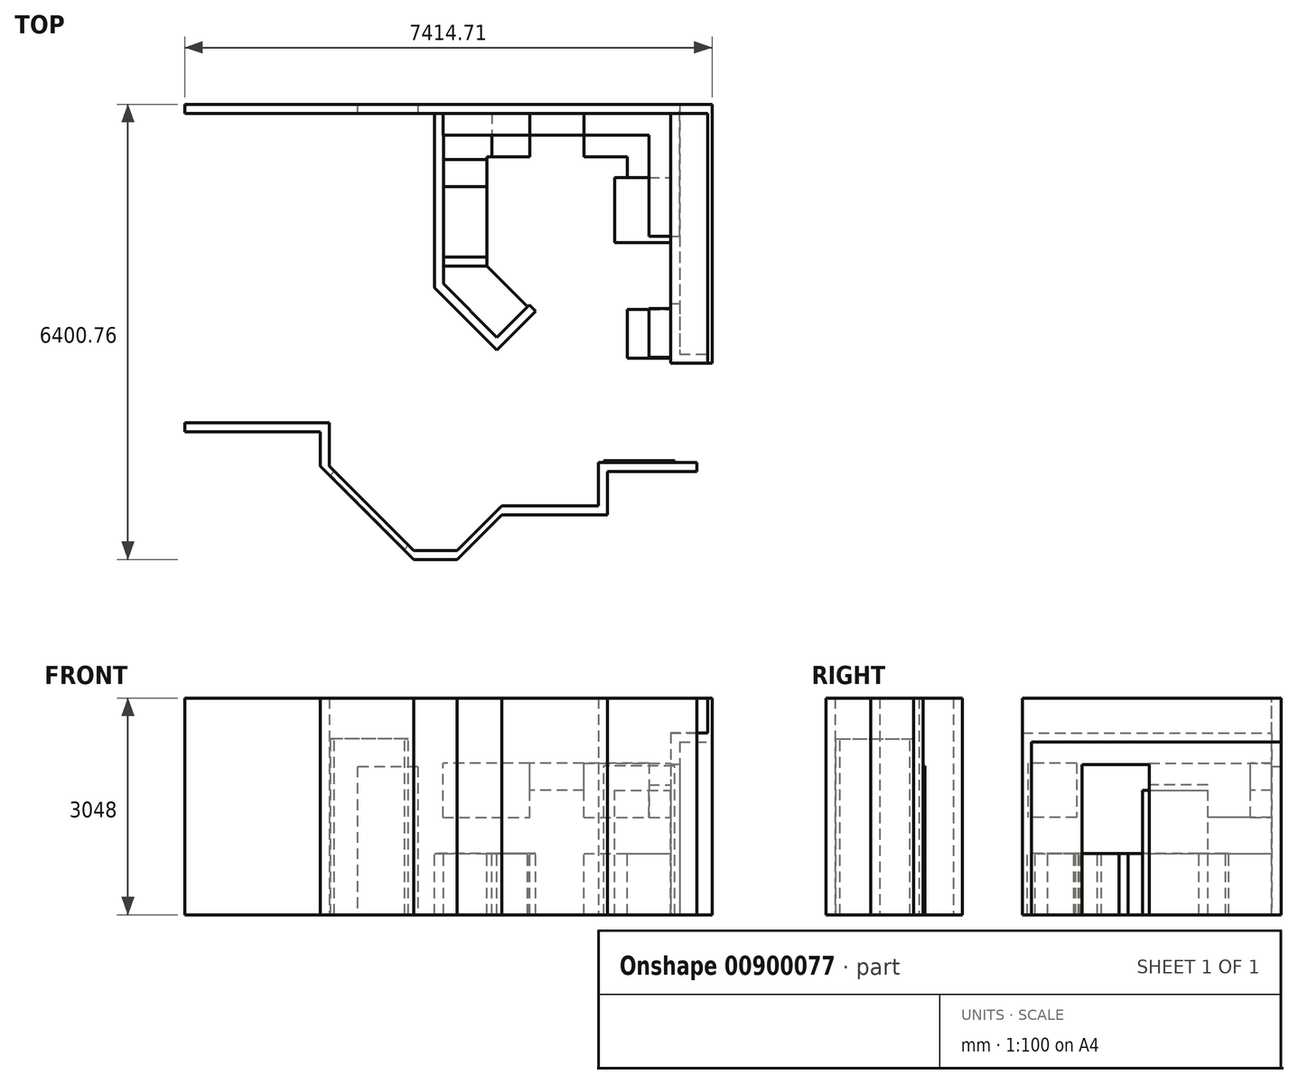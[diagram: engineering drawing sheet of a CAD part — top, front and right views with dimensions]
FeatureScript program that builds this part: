
annotation { "Feature Type Name" : "Feature", "Feature Type Description" : "" }
export const myFeature = defineFeature(function(context is Context, id is Id, definition is map)
    precondition{}
    {
        {
            var Q0;
            Q0=qCreatedBy(makeId("Top.planeOp"),FACE);
            var sketch = newSketch(context, id + "F0", { "sketchPlane" : qUnion([Q0])});
            skLineSegment(sketch, "E0.bottom", {"start": v(1769.95, -316.58) * mm, "end": v(-1786.05, -316.58) * mm});
            skLineSegment(sketch, "E0.top", {"start": v(1769.95, -189.58) * mm, "end": v(-1786.05, -189.58) * mm});
            skLineSegment(sketch, "E0.left", {"start": v(1769.95, -316.58) * mm, "end": v(1769.95, -189.58) * mm});
            skLineSegment(sketch, "E0.right", {"start": v(-1786.05, -316.58) * mm, "end": v(-1786.05, -189.58) * mm});
            skSolve(sketch);
        }
        {
            var Q0;
            Q0 = qSketchRegion(id + "F0", true);
            extrude(context, id + "F1", {"entities" : qUnion([Q0]), "depth" : 3048 * mm, "offsetDistance" : 25.4 * mm});
        }
        {
            var Q0;
            Q0=makeQuery(id+"F1.opExtrude","CAP_FACE",FACE,{"disambiguationData":[OSD([sQuery(id+"F0.wireOp",EDGE,"E0.bottom"),sQuery(id+"F0.wireOp",EDGE,"E0.top"),sQuery(id+"F0.wireOp",EDGE,"E0.left"),sQuery(id+"F0.wireOp",EDGE,"E0.right")])],"isStart":true});
            var sketch = newSketch(context, id + "F2", { "sketchPlane" : qUnion([Q0])});
            skLineSegment(sketch, "E1", {"start": v(1769.95, 316.58) * mm, "end": v(1769.95, 2043.78) * mm});
            skLineSegment(sketch, "E2", {"start": v(1769.95, 2043.78) * mm, "end": v(1896.95, 2043.78) * mm});
            skLineSegment(sketch, "E3", {"start": v(1896.95, 2043.78) * mm, "end": v(1896.95, 189.58) * mm});
            skLineSegment(sketch, "E4", {"start": v(1896.95, 189.58) * mm, "end": v(1769.95, 189.58) * mm});
            skLineSegment(sketch, "E5", {"start": v(1769.95, 189.58) * mm, "end": v(1769.95, 316.58) * mm});
            skSolve(sketch);
        }
        {
            var Q0;
            Q0=makeQuery(id+"F2.imprint","IMPRINT",FACE,{"disambiguationData":[TD([[makeQuery(id+"F2.imprint","IMPRINT",EDGE,{"derivedFrom":sQuery(id+"F2.wireOp",EDGE,"E1")}),-1.0]])]});
            var Q1;
            Q1=makeQuery(id+"F1.opExtrude","CAP_FACE",FACE,{"disambiguationData":[OSD([sQuery(id+"F0.wireOp",EDGE,"E0.bottom"),sQuery(id+"F0.wireOp",EDGE,"E0.top"),sQuery(id+"F0.wireOp",EDGE,"E0.left"),sQuery(id+"F0.wireOp",EDGE,"E0.right")])],"isStart":false});
            extrude(context, id + "F3", {"entities" : qUnion([Q0]), "operationType" : NewBodyOperationType.ADD, "endBound" : BoundingType.UP_TO_SURFACE, "oppositeDirection" : true, "depth" : 25.4 * mm, "endBoundEntityFace" : qUnion([Q1]), "offsetDistance" : 25.4 * mm});
        }
        {
            var Q0;
            Q0=makeQuery(id+"F3.boolean.opBoolean","MERGE",FACE,{"derivedFrom":[makeQuery(id+"F1.opExtrude","CAP_FACE",FACE,{"disambiguationData":[OSD([sQuery(id+"F0.wireOp",EDGE,"E0.bottom"),sQuery(id+"F0.wireOp",EDGE,"E0.top"),sQuery(id+"F0.wireOp",EDGE,"E0.left"),sQuery(id+"F0.wireOp",EDGE,"E0.right")])],"isStart":true}),makeQuery(id+"F3.opExtrude","CAP_FACE",FACE,{"disambiguationData":[OSD([sQuery(id+"F2.wireOp",EDGE,"E1"),sQuery(id+"F2.wireOp",EDGE,"E2"),sQuery(id+"F2.wireOp",EDGE,"E3"),sQuery(id+"F2.wireOp",EDGE,"E4"),sQuery(id+"F2.wireOp",EDGE,"E5")])],"isStart":true})]});
            var sketch = newSketch(context, id + "F4", { "sketchPlane" : qUnion([Q0])});
            skLineSegment(sketch, "E6", {"start": v(1769.95, 2043.78) * mm, "end": v(1769.95, 3936.08) * mm, "construction": true});
            skLineSegment(sketch, "E7", {"start": v(1896.95, 2043.78) * mm, "end": v(1896.95, 4648.91) * mm, "construction": true});
            skLineSegment(sketch, "E8.bottom", {"start": v(1769.95, 2989.93) * mm, "end": v(1896.95, 2989.93) * mm});
            skLineSegment(sketch, "E8.top", {"start": v(1769.95, 3828.13) * mm, "end": v(1896.95, 3828.13) * mm});
            skLineSegment(sketch, "E8.left", {"start": v(1769.95, 2989.93) * mm, "end": v(1769.95, 3828.13) * mm});
            skLineSegment(sketch, "E8.right", {"start": v(1896.95, 2989.93) * mm, "end": v(1896.95, 3828.13) * mm});
            skSolve(sketch);
        }
        {
            var Q0;
            Q0 = qSketchRegion(id + "F4", true);
            var Q1;
            Q1=makeQuery(id+"F3.boolean.opBoolean","MERGE",FACE,{"derivedFrom":[makeQuery(id+"F1.opExtrude","CAP_FACE",FACE,{"disambiguationData":[OSD([sQuery(id+"F0.wireOp",EDGE,"E0.bottom"),sQuery(id+"F0.wireOp",EDGE,"E0.top"),sQuery(id+"F0.wireOp",EDGE,"E0.left"),sQuery(id+"F0.wireOp",EDGE,"E0.right")])],"isStart":false}),makeQuery(id+"F3.opExtrude","CAP_FACE",FACE,{"disambiguationData":[OSD([sQuery(id+"F2.wireOp",EDGE,"E1"),sQuery(id+"F2.wireOp",EDGE,"E2"),sQuery(id+"F2.wireOp",EDGE,"E3"),sQuery(id+"F2.wireOp",EDGE,"E4"),sQuery(id+"F2.wireOp",EDGE,"E5")])],"isStart":false})]});
            extrude(context, id + "F5", {"entities" : qUnion([Q0]), "endBound" : BoundingType.UP_TO_SURFACE, "oppositeDirection" : true, "depth" : 25.4 * mm, "endBoundEntityFace" : qUnion([Q1]), "offsetDistance" : 25.4 * mm});
        }
        {
            var Q0;
            Q0=makeQuery(id+"F3.boolean.opBoolean","MERGE",FACE,{"derivedFrom":[makeQuery(id+"F1.opExtrude","CAP_FACE",FACE,{"disambiguationData":[OSD([sQuery(id+"F0.wireOp",EDGE,"E0.bottom"),sQuery(id+"F0.wireOp",EDGE,"E0.top"),sQuery(id+"F0.wireOp",EDGE,"E0.left"),sQuery(id+"F0.wireOp",EDGE,"E0.right")])],"isStart":true}),makeQuery(id+"F3.opExtrude","CAP_FACE",FACE,{"disambiguationData":[OSD([sQuery(id+"F2.wireOp",EDGE,"E1"),sQuery(id+"F2.wireOp",EDGE,"E2"),sQuery(id+"F2.wireOp",EDGE,"E3"),sQuery(id+"F2.wireOp",EDGE,"E4"),sQuery(id+"F2.wireOp",EDGE,"E5")])],"isStart":true})]});
            var sketch = newSketch(context, id + "F6", { "sketchPlane" : qUnion([Q0])});
            skLineSegment(sketch, "E9", {"start": v(1769.95, 2043.78) * mm, "end": v(1769.95, 3749.14) * mm, "construction": true});
            skLineSegment(sketch, "E10.bottom", {"start": v(1769.95, 5352.13) * mm, "end": v(753.95, 5352.13) * mm});
            skLineSegment(sketch, "E10.top", {"start": v(1769.95, 5225.13) * mm, "end": v(753.95, 5225.13) * mm});
            skLineSegment(sketch, "E10.left", {"start": v(1769.95, 5225.13) * mm, "end": v(1769.95, 5352.13) * mm});
            skLineSegment(sketch, "E10.right", {"start": v(753.95, 5225.13) * mm, "end": v(753.95, 5352.13) * mm});
            skSolve(sketch);
        }
        {
            var Q0;
            Q0=makeQuery(id+"F6.imprint","IMPRINT",FACE,{"disambiguationData":[TD([[makeQuery(id+"F6.imprint","IMPRINT",EDGE,{"derivedFrom":sQuery(id+"F6.wireOp",EDGE,"E10.bottom")}),1.0]])]});
            var Q1;
            Q1=makeQuery(id+"F3.boolean.opBoolean","MERGE",FACE,{"derivedFrom":[makeQuery(id+"F1.opExtrude","CAP_FACE",FACE,{"disambiguationData":[OSD([sQuery(id+"F0.wireOp",EDGE,"E0.bottom"),sQuery(id+"F0.wireOp",EDGE,"E0.top"),sQuery(id+"F0.wireOp",EDGE,"E0.left"),sQuery(id+"F0.wireOp",EDGE,"E0.right")])],"isStart":false}),makeQuery(id+"F3.opExtrude","CAP_FACE",FACE,{"disambiguationData":[OSD([sQuery(id+"F2.wireOp",EDGE,"E1"),sQuery(id+"F2.wireOp",EDGE,"E2"),sQuery(id+"F2.wireOp",EDGE,"E3"),sQuery(id+"F2.wireOp",EDGE,"E4"),sQuery(id+"F2.wireOp",EDGE,"E5")])],"isStart":false})]});
            extrude(context, id + "F7", {"entities" : qUnion([Q0]), "endBound" : BoundingType.UP_TO_SURFACE, "oppositeDirection" : true, "depth" : 25.4 * mm, "endBoundEntityFace" : qUnion([Q1]), "offsetDistance" : 25.4 * mm});
        }
        {
            var Q0;
            Q0=makeQuery(id+"F7.opExtrude","CAP_FACE",FACE,{"disambiguationData":[OSD([sQuery(id+"F6.wireOp",EDGE,"E10.bottom"),sQuery(id+"F6.wireOp",EDGE,"E10.top"),sQuery(id+"F6.wireOp",EDGE,"E10.left"),sQuery(id+"F6.wireOp",EDGE,"E10.right")])],"isStart":true});
            var sketch = newSketch(context, id + "F8", { "sketchPlane" : qUnion([Q0])});
            skLineSegment(sketch, "E11.bottom", {"start": v(753.95, 5225.13) * mm, "end": v(880.95, 5225.13) * mm});
            skLineSegment(sketch, "E11.top", {"start": v(753.95, 5834.73) * mm, "end": v(880.95, 5834.73) * mm});
            skLineSegment(sketch, "E11.left", {"start": v(753.95, 5225.13) * mm, "end": v(753.95, 5834.73) * mm});
            skLineSegment(sketch, "E11.right", {"start": v(880.95, 5225.13) * mm, "end": v(880.95, 5834.73) * mm});
            skLineSegment(sketch, "E12.bottom", {"start": v(880.95, 5834.73) * mm, "end": v(-604.95, 5834.73) * mm});
            skLineSegment(sketch, "E12.top", {"start": v(880.95, 5961.73) * mm, "end": v(-604.95, 5961.73) * mm});
            skLineSegment(sketch, "E12.left", {"start": v(880.95, 5834.73) * mm, "end": v(880.95, 5961.73) * mm});
            skLineSegment(sketch, "E12.right", {"start": v(-604.95, 5834.73) * mm, "end": v(-604.95, 5961.73) * mm});
            skLineSegment(sketch, "E13", {"start": v(-604.95, 5834.73) * mm, "end": v(-1233.57, 6463.34) * mm});
            skLineSegment(sketch, "E14", {"start": v(-1233.57, 6463.34) * mm, "end": v(-1843.17, 6463.34) * mm});
            skLineSegment(sketch, "E15", {"start": v(-1843.17, 6463.34) * mm, "end": v(-1843.17, 6590.34) * mm});
            skLineSegment(sketch, "E16", {"start": v(-1843.17, 6590.34) * mm, "end": v(-1233.57, 6590.34) * mm});
            skLineSegment(sketch, "E17", {"start": v(-1233.57, 6590.34) * mm, "end": v(-604.95, 5961.73) * mm});
            skLineSegment(sketch, "E18", {"start": v(-1843.17, 6463.34) * mm, "end": v(-3028.56, 5277.95) * mm});
            skLineSegment(sketch, "E19", {"start": v(-3028.56, 5277.95) * mm, "end": v(-3028.56, 4668.35) * mm});
            skLineSegment(sketch, "E20", {"start": v(-3028.56, 4668.35) * mm, "end": v(-5060.56, 4668.35) * mm});
            skLineSegment(sketch, "E21", {"start": v(-5060.56, 4668.35) * mm, "end": v(-5060.56, 4795.35) * mm});
            skLineSegment(sketch, "E22", {"start": v(-5060.56, 4795.35) * mm, "end": v(-3155.56, 4795.35) * mm});
            skLineSegment(sketch, "E23", {"start": v(-3155.56, 4795.35) * mm, "end": v(-3155.56, 5277.95) * mm});
            skLineSegment(sketch, "E24", {"start": v(-3155.56, 5277.95) * mm, "end": v(-1843.17, 6590.34) * mm});
            skSolve(sketch);
        }
        {
            var Q0;
            Q0=makeQuery(id+"F8.imprint","IMPRINT",FACE,{"disambiguationData":[TD([[makeQuery(id+"F8.imprint","IMPRINT",EDGE,{"derivedFrom":sQuery(id+"F8.wireOp",EDGE,"E15")}),1.0]])]});
            var Q1;
            Q1=makeQuery(id+"F8.imprint","IMPRINT",FACE,{"disambiguationData":[TD([[makeQuery(id+"F8.imprint","IMPRINT",EDGE,{"derivedFrom":sQuery(id+"F8.wireOp",EDGE,"E12.right")}),1.0]])]});
            var Q2;
            Q2=makeQuery(id+"F8.imprint","IMPRINT",FACE,{"disambiguationData":[TD([[makeQuery(id+"F8.imprint","IMPRINT",EDGE,{"derivedFrom":sQuery(id+"F8.wireOp",EDGE,"E12.top")}),1.0]])]});
            var Q3;
            {var subQ0=sQuery(id+"F8.wireOp",EDGE,"E11.left");var subQ1=makeQuery(id+"F7.opExtrude","CAP_EDGE",EDGE,{"disambiguationData":[OSD([sQuery(id+"F6.wireOp",EDGE,"E10.bottom")])],"isStart":true});var subQ2=makeQuery(id+"F8.imprint","INTERSECT",VERTEX,{"derivedFrom":[subQ1,subQ0]});Q3=makeQuery(id+"F8.imprint","IMPRINT",FACE,{"disambiguationData":[TD([[makeQuery(id+"F8.imprint","IMPRINT",EDGE,{"disambiguationData":[TD([[subQ2,-1.0]])],"derivedFrom":subQ0}),-1.0]])]});}
            var Q4;
            Q4=makeQuery(id+"F5.opExtrude","CAP_FACE",FACE,{"disambiguationData":[OSD([sQuery(id+"F4.wireOp",EDGE,"E8.bottom"),sQuery(id+"F4.wireOp",EDGE,"E8.top"),sQuery(id+"F4.wireOp",EDGE,"E8.left"),sQuery(id+"F4.wireOp",EDGE,"E8.right")])],"isStart":false});
            extrude(context, id + "F9", {"entities" : qUnion([Q0, Q1, Q2, Q3]), "operationType" : NewBodyOperationType.ADD, "endBound" : BoundingType.UP_TO_SURFACE, "oppositeDirection" : true, "depth" : 25.4 * mm, "endBoundEntityFace" : qUnion([Q4]), "offsetDistance" : 25.4 * mm});
        }
        {
            var Q0;
            {var subQ0=sQuery(id+"F6.wireOp",EDGE,"E10.bottom");Q0=makeQuery(id+"F9.boolean.opBoolean","MERGE",FACE,{"derivedFrom":[makeQuery(id+"F7.opExtrude","CAP_FACE",FACE,{"disambiguationData":[OSD([subQ0,sQuery(id+"F6.wireOp",EDGE,"E10.top"),sQuery(id+"F6.wireOp",EDGE,"E10.left"),sQuery(id+"F6.wireOp",EDGE,"E10.right")])],"isStart":true}),makeQuery(id+"F9.opExtrude","CAP_FACE",FACE,{"disambiguationData":[OSD([subQ0,sQuery(id+"F8.wireOp",EDGE,"E11.left"),sQuery(id+"F8.wireOp",EDGE,"E11.right"),sQuery(id+"F8.wireOp",EDGE,"E12.bottom"),sQuery(id+"F8.wireOp",EDGE,"E12.top"),sQuery(id+"F8.wireOp",EDGE,"E12.left"),sQuery(id+"F8.wireOp",EDGE,"E13"),sQuery(id+"F8.wireOp",EDGE,"E14"),sQuery(id+"F8.wireOp",EDGE,"E16"),sQuery(id+"F8.wireOp",EDGE,"E17"),sQuery(id+"F8.wireOp",EDGE,"E18"),sQuery(id+"F8.wireOp",EDGE,"E19"),sQuery(id+"F8.wireOp",EDGE,"E20"),sQuery(id+"F8.wireOp",EDGE,"E21"),sQuery(id+"F8.wireOp",EDGE,"E22"),sQuery(id+"F8.wireOp",EDGE,"E23"),sQuery(id+"F8.wireOp",EDGE,"E24")])],"isStart":true})]});}
            var sketch = newSketch(context, id + "F10", { "sketchPlane" : qUnion([Q0])});
            skLineSegment(sketch, "E25.bottom", {"start": v(1769.95, 5225.13) * mm, "end": v(2138.25, 5225.13) * mm});
            skLineSegment(sketch, "E25.top", {"start": v(1769.95, 5352.13) * mm, "end": v(2138.25, 5352.13) * mm});
            skLineSegment(sketch, "E25.left", {"start": v(1769.95, 5225.13) * mm, "end": v(1769.95, 5352.13) * mm});
            skLineSegment(sketch, "E25.right", {"start": v(2138.25, 5225.13) * mm, "end": v(2138.25, 5352.13) * mm});
            skSolve(sketch);
        }
        {
            var Q0;
            Q0=makeQuery(id+"F10.imprint","IMPRINT",FACE,{"disambiguationData":[TD([[makeQuery(id+"F10.imprint","IMPRINT",EDGE,{"derivedFrom":sQuery(id+"F10.wireOp",EDGE,"E25.bottom")}),1.0]])]});
            var Q1;
            {var subQ0=sQuery(id+"F6.wireOp",EDGE,"E10.bottom");Q1=makeQuery(id+"F9.boolean.opBoolean","MERGE",FACE,{"derivedFrom":[makeQuery(id+"F7.opExtrude","CAP_FACE",FACE,{"disambiguationData":[OSD([subQ0,sQuery(id+"F6.wireOp",EDGE,"E10.top"),sQuery(id+"F6.wireOp",EDGE,"E10.left"),sQuery(id+"F6.wireOp",EDGE,"E10.right")])],"isStart":false}),makeQuery(id+"F9.opExtrude","CAP_FACE",FACE,{"disambiguationData":[OSD([subQ0,sQuery(id+"F8.wireOp",EDGE,"E11.left"),sQuery(id+"F8.wireOp",EDGE,"E11.right"),sQuery(id+"F8.wireOp",EDGE,"E12.bottom"),sQuery(id+"F8.wireOp",EDGE,"E12.top"),sQuery(id+"F8.wireOp",EDGE,"E12.left"),sQuery(id+"F8.wireOp",EDGE,"E13"),sQuery(id+"F8.wireOp",EDGE,"E14"),sQuery(id+"F8.wireOp",EDGE,"E16"),sQuery(id+"F8.wireOp",EDGE,"E17"),sQuery(id+"F8.wireOp",EDGE,"E18"),sQuery(id+"F8.wireOp",EDGE,"E19"),sQuery(id+"F8.wireOp",EDGE,"E20"),sQuery(id+"F8.wireOp",EDGE,"E21"),sQuery(id+"F8.wireOp",EDGE,"E22"),sQuery(id+"F8.wireOp",EDGE,"E23"),sQuery(id+"F8.wireOp",EDGE,"E24")])],"isStart":false})]});}
            extrude(context, id + "F11", {"entities" : qUnion([Q0]), "operationType" : NewBodyOperationType.ADD, "endBound" : BoundingType.UP_TO_SURFACE, "oppositeDirection" : true, "depth" : 25.4 * mm, "endBoundEntityFace" : qUnion([Q1]), "offsetDistance" : 25.4 * mm});
        }
        {
            var Q0;
            Q0=makeQuery(id+"F11.boolean.opBoolean","MERGE",FACE,{"derivedFrom":[makeQuery(id+"F7.opExtrude","SWEPT_FACE",FACE,{"disambiguationData":[OSD([sQuery(id+"F6.wireOp",EDGE,"E10.top")])]}),makeQuery(id+"F11.opExtrude","SWEPT_FACE",FACE,{"disambiguationData":[OSD([sQuery(id+"F10.wireOp",EDGE,"E25.bottom")])]})]});
            var sketch = newSketch(context, id + "F12", { "sketchPlane" : qUnion([Q0])});
            skLineSegment(sketch, "E26.bottom", {"start": v(-1827.1, 0) * mm, "end": v(-830.15, 0) * mm});
            skLineSegment(sketch, "E26.top", {"start": v(-1827.1, 2095.5) * mm, "end": v(-830.15, 2095.5) * mm});
            skLineSegment(sketch, "E26.left", {"start": v(-1827.1, 0) * mm, "end": v(-1827.1, 2095.5) * mm});
            skLineSegment(sketch, "E26.right", {"start": v(-830.15, 0) * mm, "end": v(-830.15, 2095.5) * mm});
            skSolve(sketch);
        }
        {
            var Q0;
            Q0 = qSketchRegion(id + "F12", true);
            extrude(context, id + "F13", {"entities" : qUnion([Q0]), "operationType" : NewBodyOperationType.ADD, "depth" : 25.4 * mm, "offsetDistance" : 25.4 * mm});
        }
        {
            var Q0;
            Q0=makeQuery(id+"F1.opExtrude","SWEPT_FACE",FACE,{"disambiguationData":[OSD([sQuery(id+"F0.wireOp",EDGE,"E0.bottom")])]});
            var sketch = newSketch(context, id + "F14", { "sketchPlane" : qUnion([Q0])});
            skLineSegment(sketch, "E27.bottom", {"start": v(-1786.05, 3048) * mm, "end": v(-2636.95, 3048) * mm});
            skLineSegment(sketch, "E27.top", {"start": v(-1786.05, 2082.8) * mm, "end": v(-2636.95, 2082.8) * mm});
            skLineSegment(sketch, "E27.left", {"start": v(-1786.05, 3048) * mm, "end": v(-1786.05, 2082.8) * mm});
            skLineSegment(sketch, "E27.right", {"start": v(-2636.95, 3048) * mm, "end": v(-2636.95, 2082.8) * mm});
            skSolve(sketch);
        }
        {
            var Q0;
            Q0=makeQuery(id+"F14.imprint","IMPRINT",FACE,{"disambiguationData":[TD([[makeQuery(id+"F14.imprint","IMPRINT",EDGE,{"derivedFrom":sQuery(id+"F14.wireOp",EDGE,"E27.bottom")}),1.0]])]});
            var Q1;
            Q1=makeQuery(id+"F3.boolean.opBoolean","MERGE",FACE,{"derivedFrom":[makeQuery(id+"F1.opExtrude","SWEPT_FACE",FACE,{"disambiguationData":[OSD([sQuery(id+"F0.wireOp",EDGE,"E0.top")])]}),makeQuery(id+"F3.opExtrude","SWEPT_FACE",FACE,{"disambiguationData":[OSD([sQuery(id+"F2.wireOp",EDGE,"E4")])]})]});
            extrude(context, id + "F15", {"entities" : qUnion([Q0]), "operationType" : NewBodyOperationType.ADD, "endBound" : BoundingType.UP_TO_SURFACE, "oppositeDirection" : true, "depth" : 25.4 * mm, "endBoundEntityFace" : qUnion([Q1]), "offsetDistance" : 25.4 * mm});
        }
        {
            var Q0;
            Q0=makeQuery(id+"F15.opExtrude","SWEPT_FACE",FACE,{"disambiguationData":[OSD([sQuery(id+"F14.wireOp",EDGE,"E27.right")])]});
            var sketch = newSketch(context, id + "F16", { "sketchPlane" : qUnion([Q0])});
            skLineSegment(sketch, "E28.bottom", {"start": v(189.58, 3048) * mm, "end": v(316.58, 3048) * mm});
            skLineSegment(sketch, "E28.top", {"start": v(189.58, 0) * mm, "end": v(316.58, 0) * mm});
            skLineSegment(sketch, "E28.left", {"start": v(189.58, 3048) * mm, "end": v(189.58, 0) * mm});
            skLineSegment(sketch, "E28.right", {"start": v(316.58, 3048) * mm, "end": v(316.58, 0) * mm});
            skSolve(sketch);
        }
        {
            var Q0;
            {var subQ0=sQuery(id+"F16.wireOp",EDGE,"E28.bottom");Q0=makeQuery(id+"F16.imprint","IMPRINT",FACE,{"disambiguationData":[TD([[makeQuery(id+"F16.imprint","IMPRINT",EDGE,{"derivedFrom":subQ0}),-1.0]])]});}
            var Q1;
            {var subQ0=sQuery(id+"F16.wireOp",EDGE,"E28.top");Q1=makeQuery(id+"F16.imprint","IMPRINT",FACE,{"disambiguationData":[TD([[makeQuery(id+"F16.imprint","IMPRINT",EDGE,{"derivedFrom":subQ0}),1.0]])]});}
            var Q2;
            Q2=makeQuery(id+"F9.opExtrude","SWEPT_FACE",FACE,{"disambiguationData":[OSD([sQuery(id+"F8.wireOp",EDGE,"E21")])]});
            extrude(context, id + "F17", {"entities" : qUnion([Q0, Q1]), "operationType" : NewBodyOperationType.ADD, "endBound" : BoundingType.UP_TO_SURFACE, "depth" : 25.4 * mm, "endBoundEntityFace" : qUnion([Q2]), "offsetDistance" : 25.4 * mm});
        }
        {
            var Q0;
            Q0=makeQuery(id+"F3.opExtrude","SWEPT_FACE",FACE,{"disambiguationData":[OSD([sQuery(id+"F2.wireOp",EDGE,"E1"),sQuery(id+"F2.wireOp",EDGE,"E5")])]});
            var sketch = newSketch(context, id + "F18", { "sketchPlane" : qUnion([Q0])});
            skLineSegment(sketch, "E29.bottom", {"start": v(2043.78, 3048) * mm, "end": v(3103.37, 3048) * mm});
            skLineSegment(sketch, "E29.top", {"start": v(2043.78, 2114.55) * mm, "end": v(3103.37, 2114.55) * mm});
            skLineSegment(sketch, "E29.left", {"start": v(2043.78, 3048) * mm, "end": v(2043.78, 2114.55) * mm});
            skLineSegment(sketch, "E29.right", {"start": v(3103.37, 3048) * mm, "end": v(3103.37, 2114.55) * mm});
            skSolve(sketch);
        }
        {
            var Q0;
            Q0=makeQuery(id+"F18.imprint","IMPRINT",FACE,{"disambiguationData":[TD([[makeQuery(id+"F18.imprint","IMPRINT",EDGE,{"derivedFrom":sQuery(id+"F18.wireOp",EDGE,"E29.bottom")}),-1.0]])]});
            var Q1;
            Q1=makeQuery(id+"F5.opExtrude","SWEPT_FACE",FACE,{"disambiguationData":[OSD([sQuery(id+"F4.wireOp",EDGE,"E8.right")])]});
            extrude(context, id + "F19", {"entities" : qUnion([Q0]), "endBound" : BoundingType.UP_TO_SURFACE, "oppositeDirection" : true, "depth" : 25.4 * mm, "endBoundEntityFace" : qUnion([Q1]), "offsetDistance" : 25.4 * mm});
        }
        {
            var Q0;
            Q0=makeQuery(id+"F1.opExtrude","SWEPT_BODY",BODY,{"disambiguationData":[OSD([sQuery(id+"F0.wireOp",EDGE,"E0.bottom"),sQuery(id+"F0.wireOp",EDGE,"E0.top"),sQuery(id+"F0.wireOp",EDGE,"E0.left"),sQuery(id+"F0.wireOp",EDGE,"E0.right")])]});
            var Q1;
            Q1=makeQuery(id+"F19.opExtrude","SWEPT_BODY",BODY,{"disambiguationData":[OSD([sQuery(id+"F18.wireOp",EDGE,"E29.bottom"),sQuery(id+"F18.wireOp",EDGE,"E29.top"),sQuery(id+"F18.wireOp",EDGE,"E29.left"),sQuery(id+"F18.wireOp",EDGE,"E29.right")])]});
            var Q2;
            Q2=makeQuery(id+"F5.opExtrude","SWEPT_BODY",BODY,{"disambiguationData":[OSD([sQuery(id+"F4.wireOp",EDGE,"E8.bottom"),sQuery(id+"F4.wireOp",EDGE,"E8.top"),sQuery(id+"F4.wireOp",EDGE,"E8.left"),sQuery(id+"F4.wireOp",EDGE,"E8.right")])]});
            booleanBodies(context, id + "F20", {"operationType" : BooleanOperationType.UNION, "tools" : qUnion([Q0, Q1, Q2])});
        }
        {
            var Q0;
            Q0=makeQuery(id+"F20.opBoolean","MERGE",FACE,{"derivedFrom":[makeQuery(id+"F5.opExtrude","CAP_FACE",FACE,{"disambiguationData":[OSD([sQuery(id+"F4.wireOp",EDGE,"E8.bottom"),sQuery(id+"F4.wireOp",EDGE,"E8.top"),sQuery(id+"F4.wireOp",EDGE,"E8.left"),sQuery(id+"F4.wireOp",EDGE,"E8.right")])],"isStart":false}),makeQuery(id+"F17.boolean.opBoolean","MERGE",FACE,{"derivedFrom":[makeQuery(id+"F15.boolean.opBoolean","MERGE",FACE,{"derivedFrom":[makeQuery(id+"F3.boolean.opBoolean","MERGE",FACE,{"derivedFrom":[makeQuery(id+"F1.opExtrude","CAP_FACE",FACE,{"disambiguationData":[OSD([sQuery(id+"F0.wireOp",EDGE,"E0.bottom"),sQuery(id+"F0.wireOp",EDGE,"E0.top"),sQuery(id+"F0.wireOp",EDGE,"E0.left"),sQuery(id+"F0.wireOp",EDGE,"E0.right")])],"isStart":false}),makeQuery(id+"F3.opExtrude","CAP_FACE",FACE,{"disambiguationData":[OSD([sQuery(id+"F2.wireOp",EDGE,"E1"),sQuery(id+"F2.wireOp",EDGE,"E2"),sQuery(id+"F2.wireOp",EDGE,"E3"),sQuery(id+"F2.wireOp",EDGE,"E4"),sQuery(id+"F2.wireOp",EDGE,"E5")])],"isStart":false})]}),makeQuery(id+"F15.opExtrude","SWEPT_FACE",FACE,{"disambiguationData":[OSD([sQuery(id+"F14.wireOp",EDGE,"E27.bottom")])]})]}),makeQuery(id+"F17.opExtrude","SWEPT_FACE",FACE,{"disambiguationData":[OSD([sQuery(id+"F16.wireOp",EDGE,"E28.bottom")])]})]}),makeQuery(id+"F19.opExtrude","SWEPT_FACE",FACE,{"disambiguationData":[OSD([sQuery(id+"F18.wireOp",EDGE,"E29.bottom")])]})]});
            var sketch = newSketch(context, id + "F21", { "sketchPlane" : qUnion([Q0])});
            skLineSegment(sketch, "E30.bottom", {"start": v(1769.95, -3828.13) * mm, "end": v(2354.15, -3828.13) * mm});
            skLineSegment(sketch, "E30.top", {"start": v(1769.95, -3701.13) * mm, "end": v(2354.15, -3701.13) * mm});
            skLineSegment(sketch, "E30.left", {"start": v(1769.95, -3828.13) * mm, "end": v(1769.95, -3701.13) * mm});
            skLineSegment(sketch, "E30.right", {"start": v(2354.15, -3828.13) * mm, "end": v(2354.15, -3701.13) * mm});
            skSolve(sketch);
        }
        {
            var Q0;
            {var subQ3=sQuery(id+"F21.wireOp",EDGE,"E30.right");Q0=makeQuery(id+"F21.imprint","IMPRINT",FACE,{"disambiguationData":[TD([[makeQuery(id+"F21.imprint","IMPRINT",EDGE,{"derivedFrom":subQ3}),1.0]])]});}
            var Q1;
            Q1=makeQuery(id+"F5.opExtrude","CAP_FACE",FACE,{"disambiguationData":[OSD([sQuery(id+"F4.wireOp",EDGE,"E8.bottom"),sQuery(id+"F4.wireOp",EDGE,"E8.top"),sQuery(id+"F4.wireOp",EDGE,"E8.left"),sQuery(id+"F4.wireOp",EDGE,"E8.right")])],"isStart":true});
            extrude(context, id + "F22", {"entities" : qUnion([Q0]), "operationType" : NewBodyOperationType.ADD, "endBound" : BoundingType.UP_TO_SURFACE, "oppositeDirection" : true, "depth" : 25.4 * mm, "endBoundEntityFace" : qUnion([Q1]), "offsetDistance" : 25.4 * mm});
        }
        {
            var Q0;
            Q0=makeQuery(id+"F19.opExtrude","SWEPT_FACE",FACE,{"disambiguationData":[OSD([sQuery(id+"F18.wireOp",EDGE,"E29.top")])]});
            cPlane(context, id + "F23", {"entities" : qUnion([Q0]), "cplaneType" : CPlaneType.OFFSET, "offset" : 444.5 * mm, "oppositeDirection" : true, "width" : 152.4 * mm, "height" : 152.4 * mm});
        }
        {
            var Q0;
            Q0=qCreatedBy(id+"F23.planeOp",FACE);
            var sketch = newSketch(context, id + "F24", { "sketchPlane" : qUnion([Q0])});
            skLineSegment(sketch, "E31.bottom", {"start": v(1769.95, 3828.13) * mm, "end": v(2290.65, 3828.13) * mm});
            skLineSegment(sketch, "E31.top", {"start": v(1769.95, 189.58) * mm, "end": v(2290.65, 189.58) * mm});
            skLineSegment(sketch, "E31.left", {"start": v(1769.95, 3828.13) * mm, "end": v(1769.95, 189.58) * mm});
            skLineSegment(sketch, "E31.right", {"start": v(2290.65, 3828.13) * mm, "end": v(2290.65, 189.58) * mm});
            skSolve(sketch);
        }
        {
            var Q0;
            Q0=makeQuery(id+"F24.imprint","IMPRINT",FACE,{"disambiguationData":[TD([[makeQuery(id+"F24.imprint","IMPRINT",EDGE,{"derivedFrom":sQuery(id+"F24.wireOp",EDGE,"E31.bottom")}),-1.0]])]});
            extrude(context, id + "F25", {"entities" : qUnion([Q0]), "operationType" : NewBodyOperationType.ADD, "depth" : 127 * mm, "offsetDistance" : 25.4 * mm});
        }
        {
            var Q0;
            Q0=makeQuery(id+"F25.opExtrude","SWEPT_FACE",FACE,{"disambiguationData":[OSD([sQuery(id+"F24.wireOp",EDGE,"E31.right")])]});
            var sketch = newSketch(context, id + "F26", { "sketchPlane" : qUnion([Q0])});
            skLineSegment(sketch, "E32.bottom", {"start": v(-4015.8, 2559.05) * mm, "end": v(-316.58, 2559.05) * mm});
            skLineSegment(sketch, "E32.top", {"start": v(-4015.8, 4185.07) * mm, "end": v(-316.58, 4185.07) * mm});
            skLineSegment(sketch, "E32.left", {"start": v(-4015.8, 2559.05) * mm, "end": v(-4015.8, 4185.07) * mm});
            skLineSegment(sketch, "E32.right", {"start": v(-316.58, 2559.05) * mm, "end": v(-316.58, 4185.07) * mm});
            skSolve(sketch);
        }
        {
            var Q0;
            Q0 = qSketchRegion(id + "F26", true);
            extrude(context, id + "F27", {"entities" : qUnion([Q0]), "operationType" : NewBodyOperationType.REMOVE, "oppositeDirection" : true, "depth" : 1270 * mm, "offsetDistance" : 25.4 * mm});
        }
        {
            var Q0;
            Q0=makeQuery(id+"F25.boolean.opBoolean","MERGE",FACE,{"derivedFrom":[makeQuery(id+"F17.boolean.opBoolean","MERGE",FACE,{"derivedFrom":[makeQuery(id+"F15.boolean.opBoolean","MERGE",FACE,{"derivedFrom":[makeQuery(id+"F3.boolean.opBoolean","MERGE",FACE,{"derivedFrom":[makeQuery(id+"F1.opExtrude","SWEPT_FACE",FACE,{"disambiguationData":[OSD([sQuery(id+"F0.wireOp",EDGE,"E0.top")])]}),makeQuery(id+"F3.opExtrude","SWEPT_FACE",FACE,{"disambiguationData":[OSD([sQuery(id+"F2.wireOp",EDGE,"E4")])]})]}),makeQuery(id+"F15.opExtrude","CAP_FACE",FACE,{"disambiguationData":[OSD([sQuery(id+"F14.wireOp",EDGE,"E27.bottom"),sQuery(id+"F14.wireOp",EDGE,"E27.top"),sQuery(id+"F14.wireOp",EDGE,"E27.left"),sQuery(id+"F14.wireOp",EDGE,"E27.right")])],"isStart":false})]}),makeQuery(id+"F17.opExtrude","SWEPT_FACE",FACE,{"disambiguationData":[OSD([sQuery(id+"F16.wireOp",EDGE,"E28.left")])]})]}),makeQuery(id+"F25.opExtrude","SWEPT_FACE",FACE,{"disambiguationData":[OSD([sQuery(id+"F24.wireOp",EDGE,"E31.top")])]})]});
            var sketch = newSketch(context, id + "F28", { "sketchPlane" : qUnion([Q0])});
            skLineSegment(sketch, "E33.bottom", {"start": v(-1896.95, 3048) * mm, "end": v(-2354.15, 3048) * mm});
            skLineSegment(sketch, "E33.top", {"start": v(-1896.95, 2432.05) * mm, "end": v(-2354.15, 2432.05) * mm});
            skLineSegment(sketch, "E33.left", {"start": v(-1896.95, 3048) * mm, "end": v(-1896.95, 2432.05) * mm});
            skLineSegment(sketch, "E33.right", {"start": v(-2354.15, 3048) * mm, "end": v(-2354.15, 2432.05) * mm});
            skSolve(sketch);
        }
        {
            var Q0;
            {var subQ1=sQuery(id+"F28.wireOp",EDGE,"E33.bottom");Q0=makeQuery(id+"F28.imprint","IMPRINT",FACE,{"disambiguationData":[TD([[makeQuery(id+"F28.imprint","IMPRINT",EDGE,{"derivedFrom":subQ1}),1.0]])]});}
            var Q1;
            Q1=makeQuery(id+"F27.boolean.opBoolean","MERGE",FACE,{"derivedFrom":[makeQuery(id+"F17.boolean.opBoolean","MERGE",FACE,{"derivedFrom":[makeQuery(id+"F15.boolean.opBoolean","MERGE",FACE,{"derivedFrom":[makeQuery(id+"F1.opExtrude","SWEPT_FACE",FACE,{"disambiguationData":[OSD([sQuery(id+"F0.wireOp",EDGE,"E0.bottom")])]}),makeQuery(id+"F15.opExtrude","CAP_FACE",FACE,{"disambiguationData":[OSD([sQuery(id+"F14.wireOp",EDGE,"E27.bottom"),sQuery(id+"F14.wireOp",EDGE,"E27.top"),sQuery(id+"F14.wireOp",EDGE,"E27.left"),sQuery(id+"F14.wireOp",EDGE,"E27.right")])],"isStart":true})]}),makeQuery(id+"F17.opExtrude","SWEPT_FACE",FACE,{"disambiguationData":[OSD([sQuery(id+"F16.wireOp",EDGE,"E28.right")])]})]})],"fromTools":[makeQuery(id+"F27.opExtrude","SWEPT_FACE",FACE,{"disambiguationData":[OSD([sQuery(id+"F26.wireOp",EDGE,"E32.right")])]})]});
            extrude(context, id + "F29", {"entities" : qUnion([Q0]), "operationType" : NewBodyOperationType.ADD, "endBound" : BoundingType.UP_TO_SURFACE, "oppositeDirection" : true, "depth" : 25.4 * mm, "endBoundEntityFace" : qUnion([Q1]), "offsetDistance" : 25.4 * mm});
        }
        {
            var Q0;
            {var subQ0=sQuery(id+"F24.wireOp",EDGE,"E31.top");Q0=makeQuery(id+"F29.boolean.opBoolean","MERGE",FACE,{"derivedFrom":[makeQuery(id+"F25.boolean.opBoolean","MERGE",FACE,{"derivedFrom":[makeQuery(id+"F17.boolean.opBoolean","MERGE",FACE,{"derivedFrom":[makeQuery(id+"F15.boolean.opBoolean","MERGE",FACE,{"derivedFrom":[makeQuery(id+"F3.boolean.opBoolean","MERGE",FACE,{"derivedFrom":[makeQuery(id+"F1.opExtrude","SWEPT_FACE",FACE,{"disambiguationData":[OSD([sQuery(id+"F0.wireOp",EDGE,"E0.top")])]}),makeQuery(id+"F3.opExtrude","SWEPT_FACE",FACE,{"disambiguationData":[OSD([sQuery(id+"F2.wireOp",EDGE,"E4")])]})]}),makeQuery(id+"F15.opExtrude","CAP_FACE",FACE,{"disambiguationData":[OSD([sQuery(id+"F14.wireOp",EDGE,"E27.bottom"),sQuery(id+"F14.wireOp",EDGE,"E27.top"),sQuery(id+"F14.wireOp",EDGE,"E27.left"),sQuery(id+"F14.wireOp",EDGE,"E27.right")])],"isStart":false})]}),makeQuery(id+"F17.opExtrude","SWEPT_FACE",FACE,{"disambiguationData":[OSD([sQuery(id+"F16.wireOp",EDGE,"E28.left")])]})]}),makeQuery(id+"F25.opExtrude","SWEPT_FACE",FACE,{"disambiguationData":[OSD([subQ0])]})]}),makeQuery(id+"F29.opExtrude","CAP_FACE",FACE,{"disambiguationData":[OSD([subQ0,sQuery(id+"F24.wireOp",EDGE,"E31.right"),sQuery(id+"F28.wireOp",EDGE,"E33.bottom"),sQuery(id+"F28.wireOp",EDGE,"E33.top"),sQuery(id+"F28.wireOp",EDGE,"E33.left"),sQuery(id+"F28.wireOp",EDGE,"E33.right")])],"isStart":true})]});}
            var sketch = newSketch(context, id + "F30", { "sketchPlane" : qUnion([Q0])});
            skLineSegment(sketch, "E34.bottom", {"start": v(-2354.15, 3048) * mm, "end": v(-2290.65, 3048) * mm});
            skLineSegment(sketch, "E34.top", {"start": v(-2354.15, 2432.05) * mm, "end": v(-2290.65, 2432.05) * mm});
            skLineSegment(sketch, "E34.left", {"start": v(-2354.15, 3048) * mm, "end": v(-2354.15, 2432.05) * mm});
            skLineSegment(sketch, "E34.right", {"start": v(-2290.65, 3048) * mm, "end": v(-2290.65, 2432.05) * mm});
            skSolve(sketch);
        }
        {
            var Q0;
            Q0=makeQuery(id+"F30.imprint","IMPRINT",FACE,{"disambiguationData":[TD([[makeQuery(id+"F30.imprint","IMPRINT",EDGE,{"derivedFrom":sQuery(id+"F30.wireOp",EDGE,"E34.bottom")}),-1.0]])]});
            var Q1;
            Q1=makeQuery(id+"F22.opExtrude","SWEPT_FACE",FACE,{"disambiguationData":[OSD([sQuery(id+"F21.wireOp",EDGE,"E30.top")])]});
            extrude(context, id + "F31", {"entities" : qUnion([Q0]), "operationType" : NewBodyOperationType.ADD, "endBound" : BoundingType.UP_TO_SURFACE, "oppositeDirection" : true, "depth" : 25.4 * mm, "endBoundEntityFace" : qUnion([Q1]), "offsetDistance" : 25.4 * mm});
        }
        {
            var Q0;
            Q0=makeQuery(id+"F20.opBoolean","MERGE",FACE,{"derivedFrom":[makeQuery(id+"F3.opExtrude","SWEPT_FACE",FACE,{"disambiguationData":[OSD([sQuery(id+"F2.wireOp",EDGE,"E1"),sQuery(id+"F2.wireOp",EDGE,"E5")])]}),makeQuery(id+"F5.opExtrude","SWEPT_FACE",FACE,{"disambiguationData":[OSD([sQuery(id+"F4.wireOp",EDGE,"E8.left")])]}),makeQuery(id+"F19.opExtrude","CAP_FACE",FACE,{"disambiguationData":[OSD([sQuery(id+"F18.wireOp",EDGE,"E29.bottom"),sQuery(id+"F18.wireOp",EDGE,"E29.top"),sQuery(id+"F18.wireOp",EDGE,"E29.left"),sQuery(id+"F18.wireOp",EDGE,"E29.right")])],"isStart":true})]});
            var sketch = newSketch(context, id + "F32", { "sketchPlane" : qUnion([Q0])});
            skLineSegment(sketch, "E35.bottom", {"start": v(3072.48, 0) * mm, "end": v(3758.28, 0) * mm});
            skLineSegment(sketch, "E35.top", {"start": v(3072.48, 863.6) * mm, "end": v(3758.28, 863.6) * mm});
            skLineSegment(sketch, "E35.left", {"start": v(3072.48, 0) * mm, "end": v(3072.48, 863.6) * mm});
            skLineSegment(sketch, "E35.right", {"start": v(3758.28, 0) * mm, "end": v(3758.28, 863.6) * mm});
            skSolve(sketch);
        }
        {
            var Q0;
            Q0=makeQuery(id+"F32.imprint","IMPRINT",FACE,{"disambiguationData":[TD([[makeQuery(id+"F32.imprint","IMPRINT",EDGE,{"derivedFrom":sQuery(id+"F32.wireOp",EDGE,"E35.bottom")}),1.0]])]});
            extrude(context, id + "F33", {"entities" : qUnion([Q0]), "depth" : 609.6 * mm, "offsetDistance" : 25.4 * mm});
        }
        {
            var Q0;
            Q0=makeQuery(id+"F20.opBoolean","MERGE",FACE,{"derivedFrom":[makeQuery(id+"F3.opExtrude","SWEPT_FACE",FACE,{"disambiguationData":[OSD([sQuery(id+"F2.wireOp",EDGE,"E1"),sQuery(id+"F2.wireOp",EDGE,"E5")])]}),makeQuery(id+"F5.opExtrude","SWEPT_FACE",FACE,{"disambiguationData":[OSD([sQuery(id+"F4.wireOp",EDGE,"E8.left")])]}),makeQuery(id+"F19.opExtrude","CAP_FACE",FACE,{"disambiguationData":[OSD([sQuery(id+"F18.wireOp",EDGE,"E29.bottom"),sQuery(id+"F18.wireOp",EDGE,"E29.top"),sQuery(id+"F18.wireOp",EDGE,"E29.left"),sQuery(id+"F18.wireOp",EDGE,"E29.right")])],"isStart":true})]});
            var sketch = newSketch(context, id + "F34", { "sketchPlane" : qUnion([Q0])});
            skLineSegment(sketch, "E36.bottom", {"start": v(3063.44, 2133.6) * mm, "end": v(3749.24, 2133.6) * mm});
            skLineSegment(sketch, "E36.top", {"start": v(3063.44, 1371.6) * mm, "end": v(3749.24, 1371.6) * mm});
            skLineSegment(sketch, "E36.left", {"start": v(3063.44, 2133.6) * mm, "end": v(3063.44, 1371.6) * mm});
            skLineSegment(sketch, "E36.right", {"start": v(3749.24, 2133.6) * mm, "end": v(3749.24, 1371.6) * mm});
            skSolve(sketch);
        }
        {
            var Q0;
            Q0=makeQuery(id+"F34.imprint","IMPRINT",FACE,{"disambiguationData":[TD([[makeQuery(id+"F34.imprint","IMPRINT",EDGE,{"derivedFrom":sQuery(id+"F34.wireOp",EDGE,"E36.bottom")}),-1.0]])]});
            extrude(context, id + "F35", {"entities" : qUnion([Q0]), "operationType" : NewBodyOperationType.ADD, "depth" : 304.8 * mm, "offsetDistance" : 25.4 * mm});
        }
        {
            var Q0;
            Q0=makeQuery(id+"F20.opBoolean","MERGE",FACE,{"derivedFrom":[makeQuery(id+"F3.opExtrude","SWEPT_FACE",FACE,{"disambiguationData":[OSD([sQuery(id+"F2.wireOp",EDGE,"E1"),sQuery(id+"F2.wireOp",EDGE,"E5")])]}),makeQuery(id+"F5.opExtrude","SWEPT_FACE",FACE,{"disambiguationData":[OSD([sQuery(id+"F4.wireOp",EDGE,"E8.left")])]}),makeQuery(id+"F19.opExtrude","CAP_FACE",FACE,{"disambiguationData":[OSD([sQuery(id+"F18.wireOp",EDGE,"E29.bottom"),sQuery(id+"F18.wireOp",EDGE,"E29.top"),sQuery(id+"F18.wireOp",EDGE,"E29.left"),sQuery(id+"F18.wireOp",EDGE,"E29.right")])],"isStart":true})]});
            var sketch = newSketch(context, id + "F36", { "sketchPlane" : qUnion([Q0])});
            skLineSegment(sketch, "E37.bottom", {"start": v(1218.28, 0) * mm, "end": v(316.58, 0) * mm});
            skLineSegment(sketch, "E37.top", {"start": v(1218.28, 863.6) * mm, "end": v(316.58, 863.6) * mm});
            skLineSegment(sketch, "E37.left", {"start": v(1218.28, 0) * mm, "end": v(1218.28, 863.6) * mm});
            skLineSegment(sketch, "E37.right", {"start": v(316.58, 0) * mm, "end": v(316.58, 863.6) * mm});
            skSolve(sketch);
        }
        {
            var Q0;
            Q0=makeQuery(id+"F36.imprint","IMPRINT",FACE,{"disambiguationData":[TD([[makeQuery(id+"F36.imprint","IMPRINT",EDGE,{"derivedFrom":sQuery(id+"F36.wireOp",EDGE,"E37.bottom")}),1.0]])]});
            extrude(context, id + "F37", {"entities" : qUnion([Q0]), "depth" : 609.6 * mm, "offsetDistance" : 25.4 * mm});
        }
        {
            var Q0;
            Q0=makeQuery(id+"F20.opBoolean","MERGE",FACE,{"derivedFrom":[makeQuery(id+"F3.opExtrude","SWEPT_FACE",FACE,{"disambiguationData":[OSD([sQuery(id+"F2.wireOp",EDGE,"E1"),sQuery(id+"F2.wireOp",EDGE,"E5")])]}),makeQuery(id+"F5.opExtrude","SWEPT_FACE",FACE,{"disambiguationData":[OSD([sQuery(id+"F4.wireOp",EDGE,"E8.left")])]}),makeQuery(id+"F19.opExtrude","CAP_FACE",FACE,{"disambiguationData":[OSD([sQuery(id+"F18.wireOp",EDGE,"E29.bottom"),sQuery(id+"F18.wireOp",EDGE,"E29.top"),sQuery(id+"F18.wireOp",EDGE,"E29.left"),sQuery(id+"F18.wireOp",EDGE,"E29.right")])],"isStart":true})]});
            var sketch = newSketch(context, id + "F38", { "sketchPlane" : qUnion([Q0])});
            skLineSegment(sketch, "E38.bottom", {"start": v(2132.68, 0) * mm, "end": v(1218.28, 0) * mm});
            skLineSegment(sketch, "E38.top", {"start": v(2132.68, 1752.6) * mm, "end": v(1218.28, 1752.6) * mm});
            skLineSegment(sketch, "E38.left", {"start": v(2132.68, 0) * mm, "end": v(2132.68, 1752.6) * mm});
            skLineSegment(sketch, "E38.right", {"start": v(1218.28, 0) * mm, "end": v(1218.28, 1752.6) * mm});
            skSolve(sketch);
        }
        {
            var Q0;
            {var subQ4=sQuery(id+"F38.wireOp",EDGE,"E38.right");Q0=makeQuery(id+"F38.imprint","IMPRINT",FACE,{"disambiguationData":[TD([[makeQuery(id+"F38.imprint","IMPRINT",EDGE,{"derivedFrom":subQ4}),-1.0]])]});}
            var Q1;
            {var subQ3=sQuery(id+"F38.wireOp",EDGE,"E38.left");Q1=makeQuery(id+"F38.imprint","IMPRINT",FACE,{"disambiguationData":[TD([[makeQuery(id+"F38.imprint","IMPRINT",EDGE,{"derivedFrom":subQ3}),1.0]])]});}
            extrude(context, id + "F39", {"entities" : qUnion([Q0, Q1]), "depth" : 787.4 * mm, "offsetDistance" : 25.4 * mm});
        }
        {
            var Q0;
            Q0=makeQuery(id+"F29.boolean.opBoolean","MERGE",FACE,{"derivedFrom":[makeQuery(id+"F27.boolean.opBoolean","MERGE",FACE,{"derivedFrom":[makeQuery(id+"F17.boolean.opBoolean","MERGE",FACE,{"derivedFrom":[makeQuery(id+"F15.boolean.opBoolean","MERGE",FACE,{"derivedFrom":[makeQuery(id+"F1.opExtrude","SWEPT_FACE",FACE,{"disambiguationData":[OSD([sQuery(id+"F0.wireOp",EDGE,"E0.bottom")])]}),makeQuery(id+"F15.opExtrude","CAP_FACE",FACE,{"disambiguationData":[OSD([sQuery(id+"F14.wireOp",EDGE,"E27.bottom"),sQuery(id+"F14.wireOp",EDGE,"E27.top"),sQuery(id+"F14.wireOp",EDGE,"E27.left"),sQuery(id+"F14.wireOp",EDGE,"E27.right")])],"isStart":true})]}),makeQuery(id+"F17.opExtrude","SWEPT_FACE",FACE,{"disambiguationData":[OSD([sQuery(id+"F16.wireOp",EDGE,"E28.right")])]})]})],"fromTools":[makeQuery(id+"F27.opExtrude","SWEPT_FACE",FACE,{"disambiguationData":[OSD([sQuery(id+"F26.wireOp",EDGE,"E32.right")])]})]}),makeQuery(id+"F29.opExtrude","CAP_FACE",FACE,{"disambiguationData":[OSD([sQuery(id+"F24.wireOp",EDGE,"E31.top"),sQuery(id+"F24.wireOp",EDGE,"E31.right"),sQuery(id+"F28.wireOp",EDGE,"E33.bottom"),sQuery(id+"F28.wireOp",EDGE,"E33.top"),sQuery(id+"F28.wireOp",EDGE,"E33.left"),sQuery(id+"F28.wireOp",EDGE,"E33.right")])],"isStart":false})]});
            var sketch = newSketch(context, id + "F40", { "sketchPlane" : qUnion([Q0])});
            skLineSegment(sketch, "E39.bottom", {"start": v(550.75, 0) * mm, "end": v(1160.35, 0) * mm});
            skLineSegment(sketch, "E39.top", {"start": v(550.75, 863.6) * mm, "end": v(1160.35, 863.6) * mm});
            skLineSegment(sketch, "E39.left", {"start": v(550.75, 0) * mm, "end": v(550.75, 863.6) * mm});
            skLineSegment(sketch, "E39.right", {"start": v(1160.35, 0) * mm, "end": v(1160.35, 863.6) * mm});
            skSolve(sketch);
        }
        {
            var Q0;
            Q0=makeQuery(id+"F40.imprint","IMPRINT",FACE,{"disambiguationData":[TD([[makeQuery(id+"F40.imprint","IMPRINT",EDGE,{"derivedFrom":sQuery(id+"F40.wireOp",EDGE,"E39.bottom")}),-1.0]])]});
            extrude(context, id + "F41", {"entities" : qUnion([Q0]), "operationType" : NewBodyOperationType.ADD, "depth" : 609.6 * mm, "offsetDistance" : 25.4 * mm});
        }
        {
            var Q0;
            Q0=makeQuery(id+"F41.opExtrude","CAP_FACE",FACE,{"disambiguationData":[OSD([sQuery(id+"F40.wireOp",EDGE,"E39.bottom"),sQuery(id+"F40.wireOp",EDGE,"E39.top"),sQuery(id+"F40.wireOp",EDGE,"E39.left"),sQuery(id+"F40.wireOp",EDGE,"E39.right")])],"isStart":false});
            var sketch = newSketch(context, id + "F42", { "sketchPlane" : qUnion([Q0])});
            skLineSegment(sketch, "E40.bottom", {"start": v(550.75, 0) * mm, "end": v(1084.15, 0) * mm});
            skLineSegment(sketch, "E40.top", {"start": v(550.75, 863.6) * mm, "end": v(1084.15, 863.6) * mm});
            skLineSegment(sketch, "E40.left", {"start": v(550.75, 0) * mm, "end": v(550.75, 863.6) * mm});
            skLineSegment(sketch, "E40.right", {"start": v(1084.15, 0) * mm, "end": v(1084.15, 863.6) * mm});
            skSolve(sketch);
        }
        {
            var Q0;
            Q0=makeQuery(id+"F37.opExtrude","CAP_FACE",FACE,{"disambiguationData":[OSD([sQuery(id+"F36.wireOp",EDGE,"E37.bottom"),sQuery(id+"F36.wireOp",EDGE,"E37.top"),sQuery(id+"F36.wireOp",EDGE,"E37.left"),sQuery(id+"F36.wireOp",EDGE,"E37.right")])],"isStart":false});
            var sketch = newSketch(context, id + "F43", { "sketchPlane" : qUnion([Q0])});
            skLineSegment(sketch, "E41.bottom", {"start": v(989.68, 0) * mm, "end": v(1218.28, 0) * mm});
            skLineSegment(sketch, "E41.top", {"start": v(989.68, 863.6) * mm, "end": v(1218.28, 863.6) * mm});
            skLineSegment(sketch, "E41.left", {"start": v(989.68, 0) * mm, "end": v(989.68, 863.6) * mm});
            skLineSegment(sketch, "E41.right", {"start": v(1218.28, 0) * mm, "end": v(1218.28, 863.6) * mm});
            skSolve(sketch);
        }
        {
            var Q0;
            Q0=makeQuery(id+"F20.opBoolean","MERGE",FACE,{"derivedFrom":[makeQuery(id+"F3.opExtrude","SWEPT_FACE",FACE,{"disambiguationData":[OSD([sQuery(id+"F2.wireOp",EDGE,"E1"),sQuery(id+"F2.wireOp",EDGE,"E5")])]}),makeQuery(id+"F5.opExtrude","SWEPT_FACE",FACE,{"disambiguationData":[OSD([sQuery(id+"F4.wireOp",EDGE,"E8.left")])]}),makeQuery(id+"F19.opExtrude","CAP_FACE",FACE,{"disambiguationData":[OSD([sQuery(id+"F18.wireOp",EDGE,"E29.bottom"),sQuery(id+"F18.wireOp",EDGE,"E29.top"),sQuery(id+"F18.wireOp",EDGE,"E29.left"),sQuery(id+"F18.wireOp",EDGE,"E29.right")])],"isStart":true})]});
            var sketch = newSketch(context, id + "F44", { "sketchPlane" : qUnion([Q0])});
            skLineSegment(sketch, "E42", {"start": v(2043.78, 2133.6) * mm, "end": v(316.58, 2133.6) * mm});
            skLineSegment(sketch, "E43", {"start": v(316.58, 2133.6) * mm, "end": v(316.58, 1371.6) * mm});
            skLineSegment(sketch, "E44", {"start": v(316.58, 1371.6) * mm, "end": v(1218.28, 1371.6) * mm});
            skLineSegment(sketch, "E45", {"start": v(1218.28, 1371.6) * mm, "end": v(1218.28, 1828.8) * mm});
            skLineSegment(sketch, "E46", {"start": v(1218.28, 1828.8) * mm, "end": v(2043.78, 1828.8) * mm});
            skLineSegment(sketch, "E47", {"start": v(2043.78, 1828.8) * mm, "end": v(2043.78, 2133.6) * mm});
            skSolve(sketch);
        }
        {
            var Q0;
            {var subQ0=sQuery(id+"F44.wireOp",EDGE,"E42");Q0=makeQuery(id+"F44.imprint","IMPRINT",FACE,{"disambiguationData":[TD([[makeQuery(id+"F44.imprint","IMPRINT",EDGE,{"derivedFrom":subQ0}),1.0]])]});}
            var Q1;
            Q1=makeQuery(id+"F35.opExtrude","CAP_FACE",FACE,{"disambiguationData":[OSD([sQuery(id+"F34.wireOp",EDGE,"E36.bottom"),sQuery(id+"F34.wireOp",EDGE,"E36.top"),sQuery(id+"F34.wireOp",EDGE,"E36.left"),sQuery(id+"F34.wireOp",EDGE,"E36.right")])],"isStart":false});
            extrude(context, id + "F45", {"entities" : qUnion([Q0]), "endBound" : BoundingType.UP_TO_SURFACE, "depth" : 25.4 * mm, "endBoundEntityFace" : qUnion([Q1]), "offsetDistance" : 25.4 * mm});
        }
        {
            var Q0;
            Q0=makeQuery(id+"F9.opExtrude","SWEPT_FACE",FACE,{"disambiguationData":[OSD([sQuery(id+"F8.wireOp",EDGE,"E18")])]});
            var sketch = newSketch(context, id + "F46", { "sketchPlane" : qUnion([Q0])});
            skLineSegment(sketch, "E48.bottom", {"start": v(-3165.36, 0) * mm, "end": v(-1692.16, 0) * mm});
            skLineSegment(sketch, "E48.top", {"start": v(-3165.36, 2476.5) * mm, "end": v(-1692.16, 2476.5) * mm});
            skLineSegment(sketch, "E48.left", {"start": v(-3165.36, 0) * mm, "end": v(-3165.36, 2476.5) * mm});
            skLineSegment(sketch, "E48.right", {"start": v(-1692.16, 0) * mm, "end": v(-1692.16, 2476.5) * mm});
            skSolve(sketch);
        }
        {
            var Q0;
            Q0=makeQuery(id+"F46.imprint","IMPRINT",FACE,{"disambiguationData":[TD([[makeQuery(id+"F46.imprint","IMPRINT",EDGE,{"derivedFrom":sQuery(id+"F46.wireOp",EDGE,"E48.bottom")}),1.0]])]});
            extrude(context, id + "F47", {"entities" : qUnion([Q0]), "operationType" : NewBodyOperationType.REMOVE, "oppositeDirection" : true, "depth" : 76.2 * mm, "offsetDistance" : 25.4 * mm});
        }
        {
            var Q0;
            Q0=makeQuery(id+"F45.opExtrude","SWEPT_FACE",FACE,{"disambiguationData":[OSD([sQuery(id+"F44.wireOp",EDGE,"E42")])]});
            var sketch = newSketch(context, id + "F48", { "sketchPlane" : qUnion([Q0])});
            skLineSegment(sketch, "E49.bottom", {"start": v(1465.15, -316.58) * mm, "end": v(550.75, -316.58) * mm});
            skLineSegment(sketch, "E49.top", {"start": v(1465.15, -621.38) * mm, "end": v(550.75, -621.38) * mm});
            skLineSegment(sketch, "E49.left", {"start": v(1465.15, -316.58) * mm, "end": v(1465.15, -621.38) * mm});
            skLineSegment(sketch, "E49.right", {"start": v(550.75, -316.58) * mm, "end": v(550.75, -621.38) * mm});
            skSolve(sketch);
        }
        {
            var Q0;
            Q0=makeQuery(id+"F48.imprint","IMPRINT",FACE,{"disambiguationData":[TD([[makeQuery(id+"F48.imprint","IMPRINT",EDGE,{"derivedFrom":sQuery(id+"F48.wireOp",EDGE,"E49.bottom")}),1.0]])]});
            var Q1;
            Q1=makeQuery(id+"F45.opExtrude","SWEPT_FACE",FACE,{"disambiguationData":[OSD([sQuery(id+"F44.wireOp",EDGE,"E44")])]});
            extrude(context, id + "F49", {"entities" : qUnion([Q0]), "operationType" : NewBodyOperationType.ADD, "endBound" : BoundingType.UP_TO_SURFACE, "oppositeDirection" : true, "depth" : 25.4 * mm, "endBoundEntityFace" : qUnion([Q1]), "offsetDistance" : 25.4 * mm});
        }
        {
            var Q0;
            Q0=makeQuery(id+"F49.boolean.opBoolean","MERGE",FACE,{"derivedFrom":[makeQuery(id+"F45.opExtrude","SWEPT_FACE",FACE,{"disambiguationData":[OSD([sQuery(id+"F44.wireOp",EDGE,"E42")])]}),makeQuery(id+"F49.opExtrude","CAP_FACE",FACE,{"disambiguationData":[OSD([sQuery(id+"F48.wireOp",EDGE,"E49.bottom"),sQuery(id+"F48.wireOp",EDGE,"E49.top"),sQuery(id+"F48.wireOp",EDGE,"E49.left"),sQuery(id+"F48.wireOp",EDGE,"E49.right")])],"isStart":true})]});
            var sketch = newSketch(context, id + "F50", { "sketchPlane" : qUnion([Q0])});
            skLineSegment(sketch, "E50.bottom", {"start": v(550.75, -316.58) * mm, "end": v(-211.25, -316.58) * mm});
            skLineSegment(sketch, "E50.top", {"start": v(550.75, -621.38) * mm, "end": v(-211.25, -621.38) * mm});
            skLineSegment(sketch, "E50.left", {"start": v(550.75, -316.58) * mm, "end": v(550.75, -621.38) * mm});
            skLineSegment(sketch, "E50.right", {"start": v(-211.25, -316.58) * mm, "end": v(-211.25, -621.38) * mm});
            skSolve(sketch);
        }
        {
            var Q0;
            Q0=makeQuery(id+"F50.imprint","IMPRINT",FACE,{"disambiguationData":[TD([[makeQuery(id+"F50.imprint","IMPRINT",EDGE,{"derivedFrom":sQuery(id+"F50.wireOp",EDGE,"E50.bottom")}),1.0]])]});
            extrude(context, id + "F51", {"entities" : qUnion([Q0]), "oppositeDirection" : true, "depth" : 381 * mm, "offsetDistance" : 25.4 * mm});
        }
        {
            var Q0;
            Q0=makeQuery(id+"F51.opExtrude","CAP_FACE",FACE,{"disambiguationData":[OSD([sQuery(id+"F50.wireOp",EDGE,"E50.bottom"),sQuery(id+"F50.wireOp",EDGE,"E50.top"),sQuery(id+"F50.wireOp",EDGE,"E50.left"),sQuery(id+"F50.wireOp",EDGE,"E50.right")])],"isStart":true});
            var sketch = newSketch(context, id + "F52", { "sketchPlane" : qUnion([Q0])});
            skLineSegment(sketch, "E51.bottom", {"start": v(-211.25, -316.58) * mm, "end": v(-1430.45, -316.58) * mm});
            skLineSegment(sketch, "E51.top", {"start": v(-211.25, -621.38) * mm, "end": v(-1430.45, -621.38) * mm});
            skLineSegment(sketch, "E51.left", {"start": v(-211.25, -316.58) * mm, "end": v(-211.25, -621.38) * mm});
            skLineSegment(sketch, "E51.right", {"start": v(-1430.45, -316.58) * mm, "end": v(-1430.45, -621.38) * mm});
            skSolve(sketch);
        }
        {
            var Q0;
            Q0=makeQuery(id+"F52.imprint","IMPRINT",FACE,{"disambiguationData":[TD([[makeQuery(id+"F52.imprint","IMPRINT",EDGE,{"derivedFrom":sQuery(id+"F52.wireOp",EDGE,"E51.bottom")}),1.0]])]});
            var Q1;
            Q1=makeQuery(id+"F49.boolean.opBoolean","MERGE",FACE,{"derivedFrom":[makeQuery(id+"F45.opExtrude","SWEPT_FACE",FACE,{"disambiguationData":[OSD([sQuery(id+"F44.wireOp",EDGE,"E44")])]}),makeQuery(id+"F49.opExtrude","CAP_FACE",FACE,{"disambiguationData":[OSD([sQuery(id+"F48.wireOp",EDGE,"E49.bottom"),sQuery(id+"F48.wireOp",EDGE,"E49.top"),sQuery(id+"F48.wireOp",EDGE,"E49.left"),sQuery(id+"F48.wireOp",EDGE,"E49.right")])],"isStart":false})]});
            extrude(context, id + "F53", {"entities" : qUnion([Q0]), "endBound" : BoundingType.UP_TO_SURFACE, "oppositeDirection" : true, "depth" : 25.4 * mm, "endBoundEntityFace" : qUnion([Q1]), "offsetDistance" : 25.4 * mm});
        }
        {
            var Q0;
            Q0=makeQuery(id+"F41.boolean.opBoolean","MERGE",FACE,{"derivedFrom":[makeQuery(id+"F37.opExtrude","SWEPT_FACE",FACE,{"disambiguationData":[OSD([sQuery(id+"F36.wireOp",EDGE,"E37.top")])]}),makeQuery(id+"F41.opExtrude","SWEPT_FACE",FACE,{"disambiguationData":[OSD([sQuery(id+"F40.wireOp",EDGE,"E39.top")])]})]});
            var sketch = newSketch(context, id + "F54", { "sketchPlane" : qUnion([Q0])});
            skLineSegment(sketch, "E52.bottom", {"start": v(-211.25, -316.58) * mm, "end": v(-744.65, -316.58) * mm});
            skLineSegment(sketch, "E52.top", {"start": v(-211.25, -926.18) * mm, "end": v(-744.65, -926.18) * mm});
            skLineSegment(sketch, "E52.left", {"start": v(-211.25, -316.58) * mm, "end": v(-211.25, -926.18) * mm});
            skLineSegment(sketch, "E52.right", {"start": v(-744.65, -316.58) * mm, "end": v(-744.65, -926.18) * mm});
            skSolve(sketch);
        }
        {
            var Q0;
            Q0=makeQuery(id+"F54.imprint","IMPRINT",FACE,{"disambiguationData":[TD([[makeQuery(id+"F54.imprint","IMPRINT",EDGE,{"derivedFrom":sQuery(id+"F54.wireOp",EDGE,"E52.bottom")}),1.0]])]});
            var Q1;
            Q1=makeQuery(id+"F41.boolean.opBoolean","MERGE",FACE,{"derivedFrom":[makeQuery(id+"F37.opExtrude","SWEPT_FACE",FACE,{"disambiguationData":[OSD([sQuery(id+"F36.wireOp",EDGE,"E37.bottom")])]}),makeQuery(id+"F41.opExtrude","SWEPT_FACE",FACE,{"disambiguationData":[OSD([sQuery(id+"F40.wireOp",EDGE,"E39.bottom")])]})]});
            extrude(context, id + "F55", {"entities" : qUnion([Q0]), "endBound" : BoundingType.UP_TO_SURFACE, "oppositeDirection" : true, "depth" : 25.4 * mm, "endBoundEntityFace" : qUnion([Q1]), "offsetDistance" : 25.4 * mm});
        }
        {
            var Q0;
            Q0=makeQuery(id+"F55.opExtrude","CAP_FACE",FACE,{"disambiguationData":[OSD([sQuery(id+"F54.wireOp",EDGE,"E52.bottom"),sQuery(id+"F54.wireOp",EDGE,"E52.top"),sQuery(id+"F54.wireOp",EDGE,"E52.left"),sQuery(id+"F54.wireOp",EDGE,"E52.right")])],"isStart":true});
            var sketch = newSketch(context, id + "F56", { "sketchPlane" : qUnion([Q0])});
            skLineSegment(sketch, "E53", {"start": v(-744.65, -926.18) * mm, "end": v(-814.5, -926.18) * mm});
            skLineSegment(sketch, "E54", {"start": v(-814.5, -926.18) * mm, "end": v(-814.5, -964.28) * mm});
            skLineSegment(sketch, "E55", {"start": v(-814.5, -964.28) * mm, "end": v(-1424.1, -964.28) * mm});
            skLineSegment(sketch, "E56", {"start": v(-1424.1, -964.28) * mm, "end": v(-1424.1, -316.58) * mm});
            skLineSegment(sketch, "E57", {"start": v(-1424.1, -316.58) * mm, "end": v(-744.65, -316.58) * mm});
            skLineSegment(sketch, "E58", {"start": v(-744.65, -316.58) * mm, "end": v(-744.65, -926.18) * mm});
            skSolve(sketch);
        }
        {
            var Q0;
            Q0=makeQuery(id+"F56.imprint","IMPRINT",FACE,{"disambiguationData":[TD([[makeQuery(id+"F56.imprint","IMPRINT",EDGE,{"derivedFrom":sQuery(id+"F56.wireOp",EDGE,"E53")}),-1.0]])]});
            var Q1;
            Q1=makeQuery(id+"F55.opExtrude","CAP_FACE",FACE,{"disambiguationData":[OSD([sQuery(id+"F54.wireOp",EDGE,"E52.bottom"),sQuery(id+"F54.wireOp",EDGE,"E52.top"),sQuery(id+"F54.wireOp",EDGE,"E52.left"),sQuery(id+"F54.wireOp",EDGE,"E52.right")])],"isStart":false});
            extrude(context, id + "F57", {"entities" : qUnion([Q0]), "endBound" : BoundingType.UP_TO_SURFACE, "oppositeDirection" : true, "depth" : 25.4 * mm, "endBoundEntityFace" : qUnion([Q1]), "offsetDistance" : 25.4 * mm});
        }
        {
            var Q0;
            Q0=makeQuery(id+"F57.opExtrude","CAP_FACE",FACE,{"disambiguationData":[OSD([sQuery(id+"F56.wireOp",EDGE,"E53"),sQuery(id+"F56.wireOp",EDGE,"E54"),sQuery(id+"F56.wireOp",EDGE,"E55"),sQuery(id+"F56.wireOp",EDGE,"E56"),sQuery(id+"F56.wireOp",EDGE,"E57"),sQuery(id+"F56.wireOp",EDGE,"E58")])],"isStart":true});
            var sketch = newSketch(context, id + "F58", { "sketchPlane" : qUnion([Q0])});
            skLineSegment(sketch, "E59.bottom", {"start": v(-1424.1, -964.28) * mm, "end": v(-814.5, -964.28) * mm});
            skLineSegment(sketch, "E59.top", {"start": v(-1424.1, -1345.28) * mm, "end": v(-814.5, -1345.28) * mm});
            skLineSegment(sketch, "E59.left", {"start": v(-1424.1, -964.28) * mm, "end": v(-1424.1, -1345.28) * mm});
            skLineSegment(sketch, "E59.right", {"start": v(-814.5, -964.28) * mm, "end": v(-814.5, -1345.28) * mm});
            skSolve(sketch);
        }
        {
            var Q0;
            Q0=makeQuery(id+"F58.imprint","IMPRINT",FACE,{"disambiguationData":[TD([[makeQuery(id+"F58.imprint","IMPRINT",EDGE,{"derivedFrom":sQuery(id+"F58.wireOp",EDGE,"E59.bottom")}),1.0]])]});
            var Q1;
            Q1=makeQuery(id+"F57.opExtrude","CAP_FACE",FACE,{"disambiguationData":[OSD([sQuery(id+"F56.wireOp",EDGE,"E53"),sQuery(id+"F56.wireOp",EDGE,"E54"),sQuery(id+"F56.wireOp",EDGE,"E55"),sQuery(id+"F56.wireOp",EDGE,"E56"),sQuery(id+"F56.wireOp",EDGE,"E57"),sQuery(id+"F56.wireOp",EDGE,"E58")])],"isStart":false});
            extrude(context, id + "F59", {"entities" : qUnion([Q0]), "endBound" : BoundingType.UP_TO_SURFACE, "oppositeDirection" : true, "depth" : 25.4 * mm, "endBoundEntityFace" : qUnion([Q1]), "offsetDistance" : 25.4 * mm});
        }
        {
            var Q0;
            Q0=makeQuery(id+"F59.opExtrude","CAP_FACE",FACE,{"disambiguationData":[OSD([sQuery(id+"F58.wireOp",EDGE,"E59.bottom"),sQuery(id+"F58.wireOp",EDGE,"E59.top"),sQuery(id+"F58.wireOp",EDGE,"E59.left"),sQuery(id+"F58.wireOp",EDGE,"E59.right")])],"isStart":true});
            var sketch = newSketch(context, id + "F60", { "sketchPlane" : qUnion([Q0])});
            skLineSegment(sketch, "E60.bottom", {"start": v(-1424.1, -1345.28) * mm, "end": v(-814.5, -1345.28) * mm});
            skLineSegment(sketch, "E60.top", {"start": v(-1424.1, -2335.88) * mm, "end": v(-814.5, -2335.88) * mm});
            skLineSegment(sketch, "E60.left", {"start": v(-1424.1, -1345.28) * mm, "end": v(-1424.1, -2335.88) * mm});
            skLineSegment(sketch, "E60.right", {"start": v(-814.5, -1345.28) * mm, "end": v(-814.5, -2335.88) * mm});
            skSolve(sketch);
        }
        {
            var Q0;
            Q0=makeQuery(id+"F60.imprint","IMPRINT",FACE,{"disambiguationData":[TD([[makeQuery(id+"F60.imprint","IMPRINT",EDGE,{"derivedFrom":sQuery(id+"F60.wireOp",EDGE,"E60.bottom")}),-1.0]])]});
            var Q1;
            Q1=makeQuery(id+"F57.opExtrude","CAP_FACE",FACE,{"disambiguationData":[OSD([sQuery(id+"F56.wireOp",EDGE,"E53"),sQuery(id+"F56.wireOp",EDGE,"E54"),sQuery(id+"F56.wireOp",EDGE,"E55"),sQuery(id+"F56.wireOp",EDGE,"E56"),sQuery(id+"F56.wireOp",EDGE,"E57"),sQuery(id+"F56.wireOp",EDGE,"E58")])],"isStart":false});
            extrude(context, id + "F61", {"entities" : qUnion([Q0]), "endBound" : BoundingType.UP_TO_SURFACE, "oppositeDirection" : true, "depth" : 25.4 * mm, "endBoundEntityFace" : qUnion([Q1]), "offsetDistance" : 25.4 * mm});
        }
        {
            var Q0;
            Q0=makeQuery(id+"F61.opExtrude","CAP_FACE",FACE,{"disambiguationData":[OSD([sQuery(id+"F60.wireOp",EDGE,"E60.bottom"),sQuery(id+"F60.wireOp",EDGE,"E60.top"),sQuery(id+"F60.wireOp",EDGE,"E60.left"),sQuery(id+"F60.wireOp",EDGE,"E60.right")])],"isStart":true});
            var sketch = newSketch(context, id + "F62", { "sketchPlane" : qUnion([Q0])});
            skLineSegment(sketch, "E61.bottom", {"start": v(-1424.1, -2335.88) * mm, "end": v(-814.5, -2335.88) * mm});
            skLineSegment(sketch, "E61.top", {"start": v(-1424.1, -2462.88) * mm, "end": v(-814.5, -2462.88) * mm});
            skLineSegment(sketch, "E61.left", {"start": v(-1424.1, -2335.88) * mm, "end": v(-1424.1, -2462.88) * mm});
            skLineSegment(sketch, "E61.right", {"start": v(-814.5, -2335.88) * mm, "end": v(-814.5, -2462.88) * mm});
            skSolve(sketch);
        }
        {
            var Q0;
            Q0=makeQuery(id+"F62.imprint","IMPRINT",FACE,{"disambiguationData":[TD([[makeQuery(id+"F62.imprint","IMPRINT",EDGE,{"derivedFrom":sQuery(id+"F62.wireOp",EDGE,"E61.bottom")}),-1.0]])]});
            var Q1;
            Q1=makeQuery(id+"F61.opExtrude","CAP_FACE",FACE,{"disambiguationData":[OSD([sQuery(id+"F60.wireOp",EDGE,"E60.bottom"),sQuery(id+"F60.wireOp",EDGE,"E60.top"),sQuery(id+"F60.wireOp",EDGE,"E60.left"),sQuery(id+"F60.wireOp",EDGE,"E60.right")])],"isStart":false});
            extrude(context, id + "F63", {"entities" : qUnion([Q0]), "endBound" : BoundingType.UP_TO_SURFACE, "oppositeDirection" : true, "depth" : 25.4 * mm, "endBoundEntityFace" : qUnion([Q1]), "offsetDistance" : 25.4 * mm});
        }
        {
            var Q0;
            Q0=makeQuery(id+"F63.opExtrude","CAP_FACE",FACE,{"disambiguationData":[OSD([sQuery(id+"F62.wireOp",EDGE,"E61.bottom"),sQuery(id+"F62.wireOp",EDGE,"E61.top"),sQuery(id+"F62.wireOp",EDGE,"E61.left"),sQuery(id+"F62.wireOp",EDGE,"E61.right")])],"isStart":true});
            var sketch = newSketch(context, id + "F64", { "sketchPlane" : qUnion([Q0])});
            skLineSegment(sketch, "E62", {"start": v(-814.5, -2462.88) * mm, "end": v(-239.77, -3037.61) * mm});
            skLineSegment(sketch, "E63", {"start": v(-239.77, -3037.61) * mm, "end": v(-670.82, -3468.66) * mm});
            skLineSegment(sketch, "E64", {"start": v(-670.82, -3468.66) * mm, "end": v(-1424.1, -2715.38) * mm});
            skLineSegment(sketch, "E65", {"start": v(-1424.1, -2715.38) * mm, "end": v(-1424.1, -2462.88) * mm});
            skLineSegment(sketch, "E66", {"start": v(-1424.1, -2462.88) * mm, "end": v(-814.5, -2462.88) * mm});
            skSolve(sketch);
        }
        {
            var Q0;
            Q0=makeQuery(id+"F64.imprint","IMPRINT",FACE,{"disambiguationData":[TD([[makeQuery(id+"F64.imprint","IMPRINT",EDGE,{"derivedFrom":sQuery(id+"F64.wireOp",EDGE,"E62")}),-1.0]])]});
            var Q1;
            Q1=makeQuery(id+"F63.opExtrude","CAP_FACE",FACE,{"disambiguationData":[OSD([sQuery(id+"F62.wireOp",EDGE,"E61.bottom"),sQuery(id+"F62.wireOp",EDGE,"E61.top"),sQuery(id+"F62.wireOp",EDGE,"E61.left"),sQuery(id+"F62.wireOp",EDGE,"E61.right")])],"isStart":false});
            extrude(context, id + "F65", {"entities" : qUnion([Q0]), "endBound" : BoundingType.UP_TO_SURFACE, "oppositeDirection" : true, "depth" : 25.4 * mm, "endBoundEntityFace" : qUnion([Q1]), "offsetDistance" : 25.4 * mm});
        }
        {
            var Q0;
            Q0=makeQuery(id+"F65.opExtrude","CAP_FACE",FACE,{"disambiguationData":[OSD([sQuery(id+"F64.wireOp",EDGE,"E62"),sQuery(id+"F64.wireOp",EDGE,"E63"),sQuery(id+"F64.wireOp",EDGE,"E64"),sQuery(id+"F64.wireOp",EDGE,"E65"),sQuery(id+"F64.wireOp",EDGE,"E66")])],"isStart":true});
            var sketch = newSketch(context, id + "F66", { "sketchPlane" : qUnion([Q0])});
            skLineSegment(sketch, "E67", {"start": v(-239.77, -3037.61) * mm, "end": v(-212.83, -3010.67) * mm});
            skLineSegment(sketch, "E68", {"start": v(-212.83, -3010.67) * mm, "end": v(-123.02, -3100.47) * mm});
            skLineSegment(sketch, "E69", {"start": v(-123.02, -3100.47) * mm, "end": v(-670.82, -3648.27) * mm});
            skLineSegment(sketch, "E70", {"start": v(-670.82, -3648.27) * mm, "end": v(-1551.1, -2767.98) * mm});
            skLineSegment(sketch, "E71", {"start": v(-1551.1, -2767.98) * mm, "end": v(-1551.1, -316.58) * mm});
            skLineSegment(sketch, "E72", {"start": v(-1551.1, -316.58) * mm, "end": v(-1424.1, -316.58) * mm});
            skLineSegment(sketch, "E73", {"start": v(-1424.1, -316.58) * mm, "end": v(-1424.1, -2715.38) * mm});
            skLineSegment(sketch, "E74", {"start": v(-1424.1, -2715.38) * mm, "end": v(-670.82, -3468.66) * mm});
            skLineSegment(sketch, "E75", {"start": v(-670.82, -3468.66) * mm, "end": v(-239.77, -3037.61) * mm});
            skSolve(sketch);
        }
        {
            var Q0;
            Q0=makeQuery(id+"F66.imprint","IMPRINT",FACE,{"disambiguationData":[TD([[makeQuery(id+"F66.imprint","IMPRINT",EDGE,{"derivedFrom":sQuery(id+"F66.wireOp",EDGE,"E67")}),-1.0]])]});
            var Q1;
            Q1=makeQuery(id+"F3.boolean.opBoolean","MERGE",FACE,{"derivedFrom":[makeQuery(id+"F1.opExtrude","CAP_FACE",FACE,{"disambiguationData":[OSD([sQuery(id+"F0.wireOp",EDGE,"E0.bottom"),sQuery(id+"F0.wireOp",EDGE,"E0.top"),sQuery(id+"F0.wireOp",EDGE,"E0.left"),sQuery(id+"F0.wireOp",EDGE,"E0.right")])],"isStart":true}),makeQuery(id+"F3.opExtrude","CAP_FACE",FACE,{"disambiguationData":[OSD([sQuery(id+"F2.wireOp",EDGE,"E1"),sQuery(id+"F2.wireOp",EDGE,"E2"),sQuery(id+"F2.wireOp",EDGE,"E3"),sQuery(id+"F2.wireOp",EDGE,"E4"),sQuery(id+"F2.wireOp",EDGE,"E5")])],"isStart":true})]});
            extrude(context, id + "F67", {"entities" : qUnion([Q0]), "endBound" : BoundingType.UP_TO_SURFACE, "oppositeDirection" : true, "depth" : 25.4 * mm, "endBoundEntityFace" : qUnion([Q1]), "offsetDistance" : 25.4 * mm});
        }
    });
